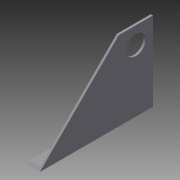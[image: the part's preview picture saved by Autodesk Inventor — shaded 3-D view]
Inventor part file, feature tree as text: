
AUTODESK INVENTOR PART (.ipt)
format: ipt  version: 2013 (Build 170138000, 138)  size: 91,136 bytes
history: native  units: in
note: dims shown in document units (in); Inventor stores cm internally (conversion verified against a paired STEP export)
features: extrude x2, sketch x2
ambient origin geometry x8: Origin, YZ Plane, XZ Plane, XY Plane, X Axis, Y Axis, Z Axis, Center Point
bodies: Solid1 (feature_tree)
feature tree (4):
  extrude  "Extrusion1"  TaperAngle=0.0deg  [1 undecoded]
  extrude  "Extrusion2"  Depth=1.0in
  sketch  "Sketch1"  dims[d0=3.625in d1=0.0in]
  sketch  "Sketch2"  dims[d2=1.125in d3=1.0in d4=0.0in d5=1.0in d6=90.0deg d7=1.0in d8=90.0deg d9=135.0deg d10=0.125in d11=0.0in d12=0.125in d13=90.0deg d14=0.625in d15=0.0in]
note: 1 required parameter value undecoded (feature->parameter linkage not recoverable at this tier; creation-order binding heuristic only, values carry confidence <= 0.55)
